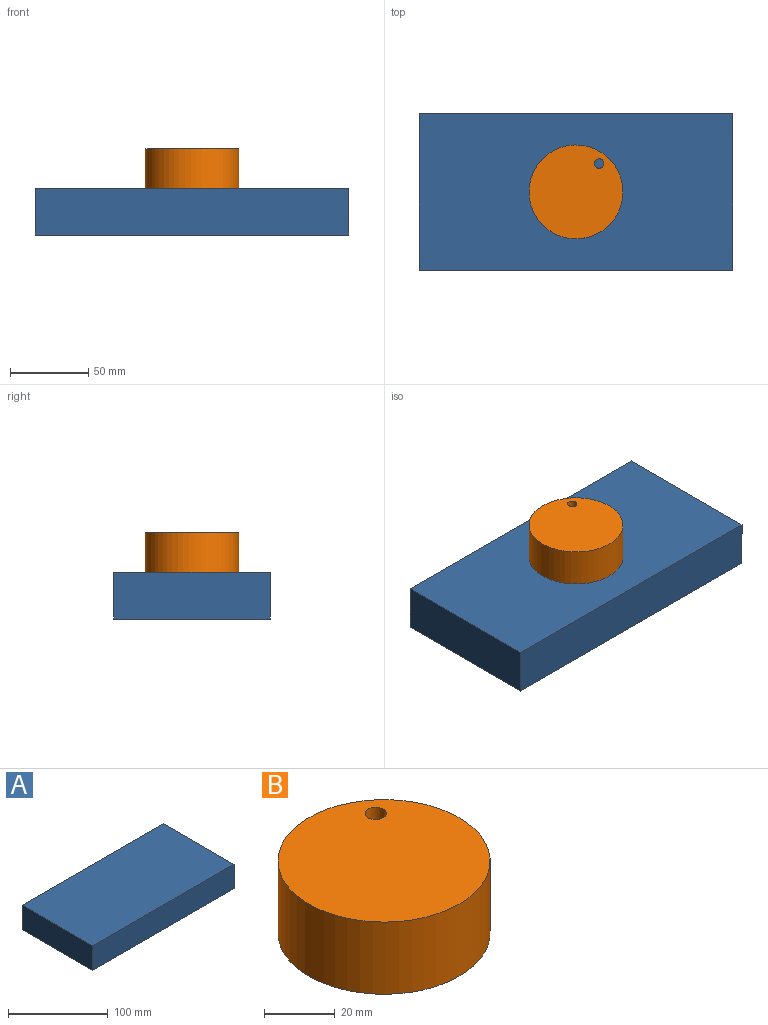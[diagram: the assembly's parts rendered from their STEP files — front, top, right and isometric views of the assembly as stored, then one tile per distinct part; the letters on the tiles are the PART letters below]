
ASSEMBLY  parts=2 mates=1
PART A: 6 faces, bbox 200x100x30 mm
  f0: plane 200x30mm, normal (0,-1,0), area 6000mm2, adj f1,f3,f4,f5
  f1: plane 100x30mm, normal (1,0,0), area 3000mm2, adj f0,f2,f4,f5
  f2: plane 200x30mm, normal (0,1,0), area 6000mm2, adj f1,f3,f4,f5
  f3: plane 100x30mm, normal (-1,0,0), area 3000mm2, adj f0,f2,f4,f5
  f4: plane 200x100mm, normal (0,0,1), area 20000mm2, adj f0,f1,f2,f3
  f5: plane 200x100mm, normal (0,0,-1), area 20000mm2, adj f0,f1,f2,f3
PART B: 4 faces, bbox 60x60x25 mm
  f0: cylinder r=3mm len=25mm, axis (0,0,-1), area 471.2mm2, adj f2,f3
  f1: cylinder r=30mm len=60mm, axis (0,0,-1), area 4712.4mm2, adj f2,f3
  f2: plane 60x60mm, normal (0,0,1), area 2799.2mm2, adj f0,f1
  f3: plane 60x60mm, normal (0,0,-1), area 2799.2mm2, adj f0,f1
PLACE A rot(axis=(-0.68,-0.17,-0.72),0deg) t=(0,0,0)mm
PLACE B at identity
MATE cylindrical B.f1 <-> A.f4  axis (0,0,-1) through (-100,50,30)mm
